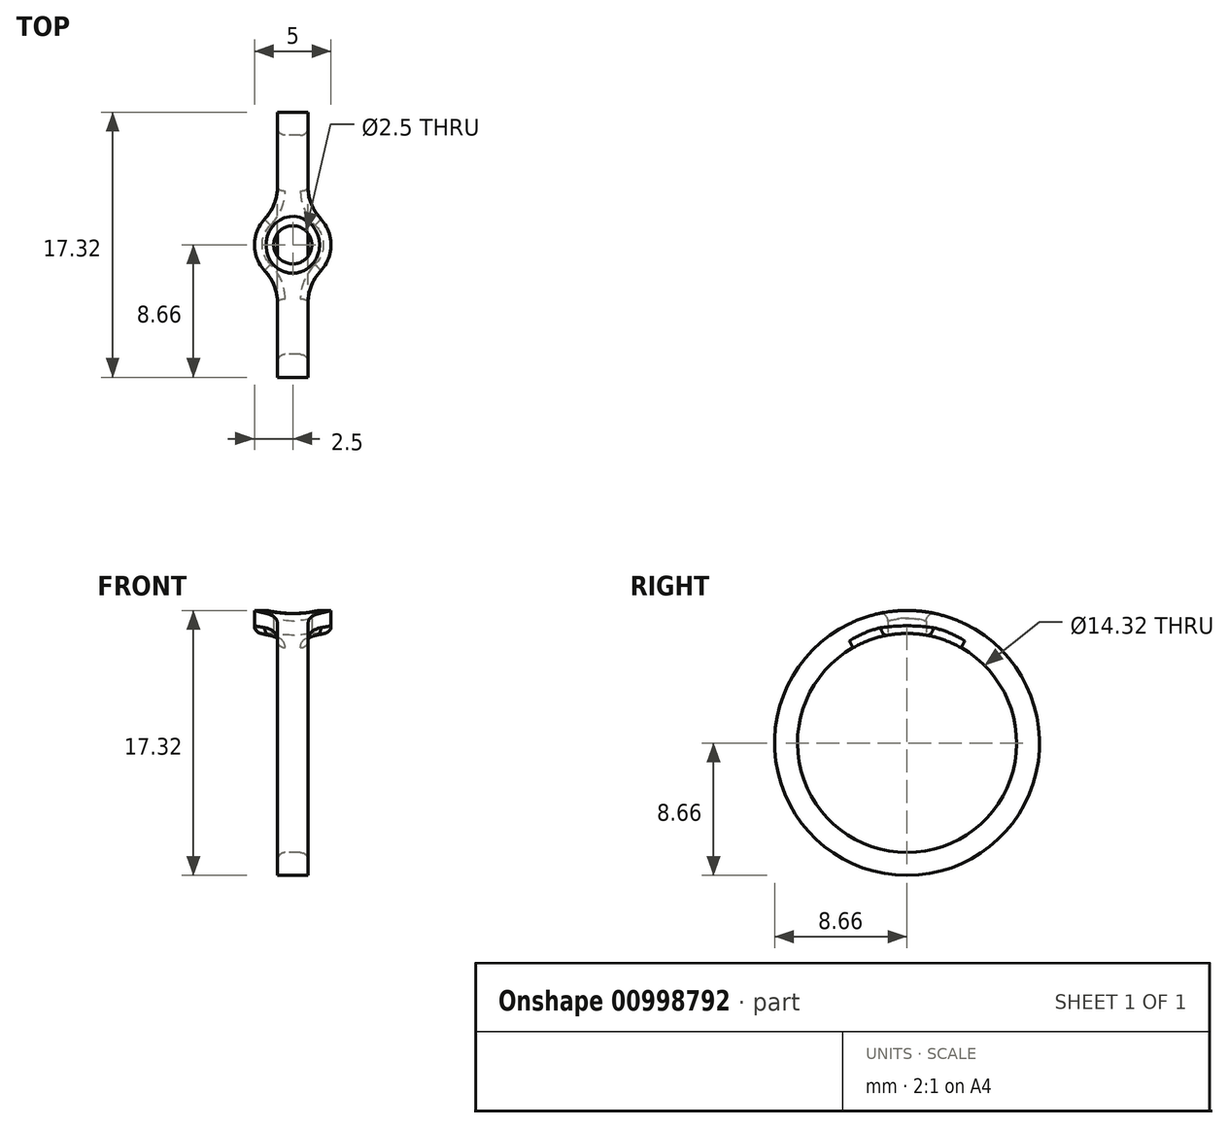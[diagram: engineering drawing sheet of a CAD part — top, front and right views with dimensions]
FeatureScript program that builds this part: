
annotation { "Feature Type Name" : "Feature", "Feature Type Description" : "" }
export const myFeature = defineFeature(function(context is Context, id is Id, definition is map)
    precondition{}
    {
        {
            var Q0;
            Q0=qCreatedBy(makeId("Front.planeOp"),FACE);
            var sketch = newSketch(context, id + "F0", { "sketchPlane" : qUnion([Q0])});
            skLineSegment(sketch, "E0", {"start": v(-2.5, 7.16) * mm, "end": v(2.5, 7.16) * mm});
            skLineSegment(sketch, "E1", {"start": v(-2.5, 7.16) * mm, "end": v(-2.5, 8.66) * mm});
            skLineSegment(sketch, "E2", {"start": v(2.5, 8.66) * mm, "end": v(2.5, 7.16) * mm});
            skLineSegment(sketch, "E3", {"start": v(-6, 0) * mm, "end": v(8.43, 0) * mm});
            skLineSegment(sketch, "E4", {"start": v(-2.5, 8.66) * mm, "end": v(2.5, 8.66) * mm});
            skSolve(sketch);
        }
        {
            var Q0;
            Q0=makeQuery(id+"F0.imprint","IMPRINT",FACE,{"disambiguationData":[TD([[makeQuery(id+"F0.imprint","IMPRINT",EDGE,{"derivedFrom":sQuery(id+"F0.wireOp",EDGE,"E0")}),1.0]])]});
            var Q1;
            Q1=sQuery(id+"F0.wireOp",EDGE,"E3");
            revolve(context, id + "F1", {"surfaceOperationType" : NewSurfaceOperationType.NEW, "entities" : qUnion([Q0]), "axis" : qUnion([Q1]), "revolveType" : RevolveType.FULL});
        }
        {
            var Q0;
            Q0=qCreatedBy(makeId("Top.planeOp"),FACE);
            var sketch = newSketch(context, id + "F2", { "sketchPlane" : qUnion([Q0])});
            skCircle(sketch, "E5", {"center": v(0, 0) * mm, "radius": 1.25 * mm});
            skArc(sketch, "E6", {"start": v(1.82, -1.72) * mm, "mid": v(2.5, 0) * mm, "end": v(1.82, 1.72) * mm});
            skLineSegment(sketch, "E7.left", {"start": v(-1, 13.8) * mm, "end": v(-1, 3.77) * mm});
            skLineSegment(sketch, "E7.right", {"start": v(1, 13.8) * mm, "end": v(1, 3.77) * mm});
            skLineSegment(sketch, "E8.bottom", {"start": v(-4.3, 13.8) * mm, "end": v(-1, 13.8) * mm});
            skLineSegment(sketch, "E8.top", {"start": v(-4.3, -10.56) * mm, "end": v(-1, -10.56) * mm});
            skLineSegment(sketch, "E8.left", {"start": v(-4.3, 13.8) * mm, "end": v(-4.3, -10.56) * mm});
            skLineSegment(sketch, "E8.right", {"start": v(5.06, 13.8) * mm, "end": v(5.06, -10.56) * mm});
            skLineSegment(sketch, "E9.trimOffspring", {"start": v(1, 13.8) * mm, "end": v(5.06, 13.8) * mm});
            skLineSegment(sketch, "E10.trimOffspring", {"start": v(1, -10.56) * mm, "end": v(5.06, -10.56) * mm});
            skPoint(sketch, "E7.top.start.orphan", {"position": v(-1, -12.7) * mm});
            skLineSegment(sketch, "E11.trimOffspring", {"start": v(-1, -3.77) * mm, "end": v(-1, -10.56) * mm});
            skLineSegment(sketch, "E12.trimOffspring", {"start": v(1, -3.77) * mm, "end": v(1, -10.56) * mm});
            skArc(sketch, "E13.trimOffspring", {"start": v(-1.82, 1.72) * mm, "mid": v(-2.5, 0) * mm, "end": v(-1.82, -1.72) * mm});
            skPoint(sketch, "E14.visualSharp", {"position": v(-1, 2.3) * mm});
            skArc(sketch, "E14.filletArc", {"start": v(-1.82, 1.72) * mm, "mid": v(-1.21, 2.67) * mm, "end": v(-1, 3.77) * mm});
            skPoint(sketch, "E15.visualSharp", {"position": v(1, 2.3) * mm});
            skArc(sketch, "E15.filletArc", {"start": v(1, 3.77) * mm, "mid": v(1.21, 2.67) * mm, "end": v(1.82, 1.72) * mm});
            skPoint(sketch, "E16.visualSharp", {"position": v(-1, -2.3) * mm});
            skArc(sketch, "E16.filletArc", {"start": v(-1, -3.77) * mm, "mid": v(-1.21, -2.67) * mm, "end": v(-1.82, -1.72) * mm});
            skPoint(sketch, "E17.visualSharp", {"position": v(1, -2.3) * mm});
            skArc(sketch, "E17.filletArc", {"start": v(1.82, -1.72) * mm, "mid": v(1.21, -2.67) * mm, "end": v(1, -3.77) * mm});
            skSolve(sketch);
        }
        {
            var Q0;
            Q0=makeQuery(id+"F2.imprint","IMPRINT",FACE,{"disambiguationData":[TD([[makeQuery(id+"F2.imprint","IMPRINT",EDGE,{"derivedFrom":sQuery(id+"F2.wireOp",EDGE,"E7.left")}),-1.0]])]});
            var Q1;
            Q1=makeQuery(id+"F2.imprint","IMPRINT",FACE,{"disambiguationData":[TD([[makeQuery(id+"F2.imprint","IMPRINT",EDGE,{"derivedFrom":sQuery(id+"F2.wireOp",EDGE,"E6")}),-1.0]])]});
            var Q2;
            Q2=makeQuery(id+"F2.imprint","IMPRINT",FACE,{"disambiguationData":[TD([[makeQuery(id+"F2.imprint","IMPRINT",EDGE,{"derivedFrom":sQuery(id+"F2.wireOp",EDGE,"E5")}),1.0]])]});
            extrude(context, id + "F3", {"entities" : qUnion([Q0, Q1, Q2]), "operationType" : NewBodyOperationType.REMOVE, "endBound" : BoundingType.THROUGH_ALL, "depth" : 25 * mm, "offsetDistance" : 25 * mm});
        }
        {
            var Q0;
            Q0=qCreatedBy(makeId("Top.planeOp"),FACE);
            var sketch = newSketch(context, id + "F4", { "sketchPlane" : qUnion([Q0])});
            skLineSegment(sketch, "E18.left", {"start": v(-1, 10.42) * mm, "end": v(-1, -9.56) * mm});
            skLineSegment(sketch, "E18.right", {"start": v(1, 10.42) * mm, "end": v(1, -9.56) * mm});
            skLineSegment(sketch, "E19.bottom", {"start": v(-4.56, 10.42) * mm, "end": v(-1, 10.42) * mm});
            skLineSegment(sketch, "E19.top", {"start": v(-4.56, -9.56) * mm, "end": v(-1, -9.56) * mm});
            skLineSegment(sketch, "E19.left", {"start": v(-4.56, 10.42) * mm, "end": v(-4.56, -9.56) * mm});
            skLineSegment(sketch, "E19.right", {"start": v(3.22, 10.42) * mm, "end": v(3.22, -9.56) * mm});
            skLineSegment(sketch, "E20.trimOffspring", {"start": v(1, -9.56) * mm, "end": v(3.22, -9.56) * mm});
            skLineSegment(sketch, "E21.trimOffspring", {"start": v(1, 10.42) * mm, "end": v(3.22, 10.42) * mm});
            skSolve(sketch);
        }
        {
            var Q0;
            Q0=makeQuery(id+"F4.imprint","IMPRINT",FACE,{"disambiguationData":[TD([[makeQuery(id+"F4.imprint","IMPRINT",EDGE,{"derivedFrom":sQuery(id+"F4.wireOp",EDGE,"E18.left")}),-1.0]])]});
            var Q1;
            Q1=makeQuery(id+"F4.imprint","IMPRINT",FACE,{"disambiguationData":[TD([[makeQuery(id+"F4.imprint","IMPRINT",EDGE,{"derivedFrom":sQuery(id+"F4.wireOp",EDGE,"E18.right")}),1.0]])]});
            extrude(context, id + "F5", {"entities" : qUnion([Q0, Q1]), "operationType" : NewBodyOperationType.REMOVE, "oppositeDirection" : true, "depth" : 25 * mm, "offsetDistance" : 25 * mm});
        }
        {
            var Q0;
            Q0=makeQuery(id+"F5.boolean.opBoolean","INTERSECT",EDGE,{"derivedFrom":[makeQuery(id+"F1.opRevolve","SWEPT_FACE",FACE,{"disambiguationData":[OSD([sQuery(id+"F0.wireOp",EDGE,"E0")])]}),makeQuery(id+"F5.opExtrude","SWEPT_FACE",FACE,{"disambiguationData":[OSD([sQuery(id+"F4.wireOp",EDGE,"E18.right")])]})]});
            var Q1;
            Q1=makeQuery(id+"F5.boolean.opBoolean","INTERSECT",EDGE,{"derivedFrom":[makeQuery(id+"F1.opRevolve","SWEPT_FACE",FACE,{"disambiguationData":[OSD([sQuery(id+"F0.wireOp",EDGE,"E0")])]}),makeQuery(id+"F5.opExtrude","SWEPT_FACE",FACE,{"disambiguationData":[OSD([sQuery(id+"F4.wireOp",EDGE,"E18.left")])]})]});
            fillet(context, id + "F6", {"entities" : qUnion([Q0, Q1]), "radius" : 0.5 * mm, "tangentPropagation" : true, "allowEdgeOverflow" : false});
        }
        {
            var Q0;
            Q0=makeQuery(id+"F5.boolean.opBoolean","INTERSECT",EDGE,{"derivedFrom":[makeQuery(id+"F1.opRevolve","SWEPT_FACE",FACE,{"disambiguationData":[OSD([sQuery(id+"F0.wireOp",EDGE,"oR7hY7NQ-Qn57-Ni2P-JsMY-QIJTek8WU6Yr")])]}),makeQuery(id+"F5.opExtrude","SWEPT_FACE",FACE,{"disambiguationData":[OSD([sQuery(id+"F4.wireOp",EDGE,"E18.left")])]})]});
            var Q1;
            Q1=makeQuery(id+"F3.boolean.opBoolean","INTERSECT",EDGE,{"derivedFrom":[makeQuery(id+"F1.opRevolve","SWEPT_FACE",FACE,{"disambiguationData":[OSD([sQuery(id+"F0.wireOp",EDGE,"oR7hY7NQ-Qn57-Ni2P-JsMY-QIJTek8WU6Yr")])]}),makeQuery(id+"F3.opExtrude","SWEPT_FACE",FACE,{"disambiguationData":[OSD([sQuery(id+"F2.wireOp",EDGE,"E17.filletArc")])]})]});
            var Q2;
            Q2=makeQuery(id+"F3.boolean.opBoolean","INTERSECT",EDGE,{"derivedFrom":[makeQuery(id+"F1.opRevolve","SWEPT_FACE",FACE,{"disambiguationData":[OSD([sQuery(id+"F0.wireOp",EDGE,"E4")])]}),makeQuery(id+"F3.opExtrude","SWEPT_FACE",FACE,{"disambiguationData":[OSD([sQuery(id+"F2.wireOp",EDGE,"E5")])]})]});
            fillet(context, id + "F7", {"entities" : qUnion([Q0, Q1, Q2]), "radius" : 0.5 * mm, "tangentPropagation" : true, "allowEdgeOverflow" : false});
        }
    });
